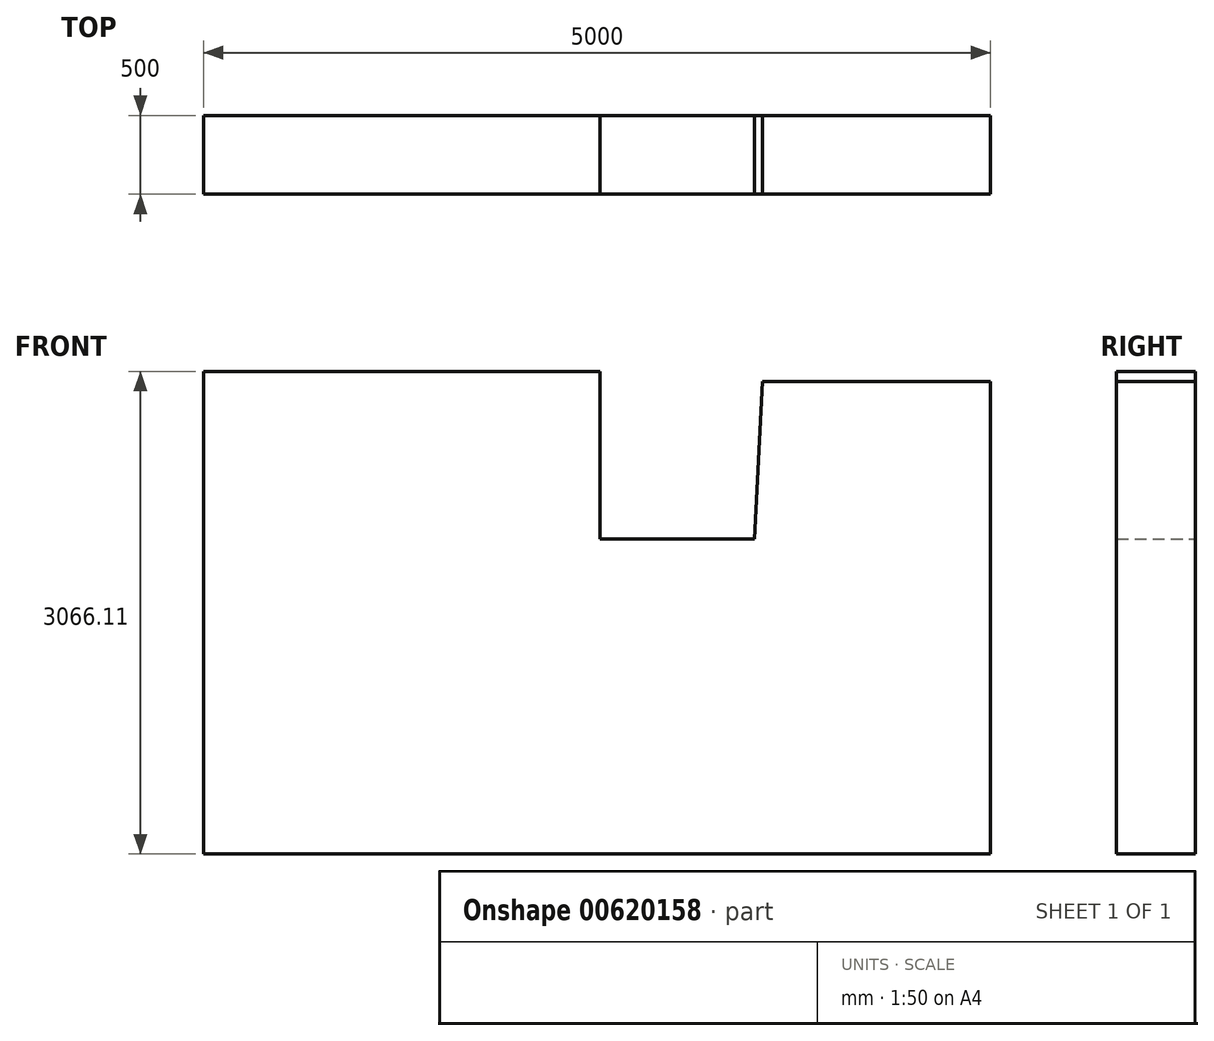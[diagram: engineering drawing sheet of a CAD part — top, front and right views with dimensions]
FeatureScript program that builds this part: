
annotation { "Feature Type Name" : "Feature", "Feature Type Description" : "" }
export const myFeature = defineFeature(function(context is Context, id is Id, definition is map)
    precondition{}
    {
        {
            var Q0;
            Q0=qCreatedBy(makeId("Front.planeOp"),FACE);
            var sketch = newSketch(context, id + "F0", { "sketchPlane" : qUnion([Q0])});
            skLineSegment(sketch, "E0", {"start": v(-2581.64, 1611.81) * mm, "end": v(-61.64, 1611.81) * mm});
            skLineSegment(sketch, "E1", {"start": v(-61.64, 1611.81) * mm, "end": v(-61.64, 545.7) * mm});
            skLineSegment(sketch, "E2", {"start": v(-61.64, 545.7) * mm, "end": v(918.36, 545.7) * mm});
            skLineSegment(sketch, "E3", {"start": v(918.36, 545.7) * mm, "end": v(968.36, 1545.7) * mm});
            skLineSegment(sketch, "E4", {"start": v(968.36, 1545.7) * mm, "end": v(2418.36, 1545.7) * mm});
            skLineSegment(sketch, "E5", {"start": v(2418.36, 1545.7) * mm, "end": v(2418.36, -1454.3) * mm});
            skLineSegment(sketch, "E6", {"start": v(2418.36, -1454.3) * mm, "end": v(-2581.64, -1454.3) * mm});
            skLineSegment(sketch, "E7", {"start": v(-2581.64, -1454.3) * mm, "end": v(-2581.64, 1611.81) * mm});
            skSolve(sketch);
        }
        {
            var Q0;
            Q0 = qSketchRegion(id + "F0", true);
            extrude(context, id + "F1", {"entities" : qUnion([Q0]), "depth" : 500 * mm, "offsetDistance" : 25 * mm});
        }
    });
